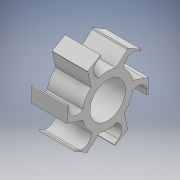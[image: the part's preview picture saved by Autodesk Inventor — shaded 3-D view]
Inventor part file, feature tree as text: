
AUTODESK INVENTOR PART (.ipt)
format: ipt  version: 2018 (Build 220112000, 112)  size: 352,768 bytes
history: native  units: mm
features: extrude x2, sketch x2, fillet x1, pattern_circular x1
ambient origin geometry x8: Origin, YZ Plane, XZ Plane, XY Plane, X Axis, Y Axis, Z Axis, Center Point
bodies: Solid1 (feature_tree)
feature tree (6):
  extrude  "Extrusion1"  Depth=3.5mm
  extrude  "Extrusion2"  Depth=0.125mm
  fillet  "Fillet1"  Radius=0.25mm
  pattern_circular  "Circular Pattern1"  [2 undecoded]
  sketch  "Sketch1"  dims[d0=3.5mm d1=5.0mm]
  sketch  "Sketch2"  dims[d2=3.5mm d3=0.0mm d4=0.125mm d5=0.25mm d6=0.5mm d11=0.5mm d12=1.0mm d14=1.0mm d15=0.9mm d16=1.5mm d17=0.125mm d18=3.5mm d19=0.0mm d20=2.0mm d21=60.0mm d22=360.0deg]
note: 2 required parameter values undecoded (feature->parameter linkage not recoverable at this tier; creation-order binding heuristic only, values carry confidence <= 0.55)
